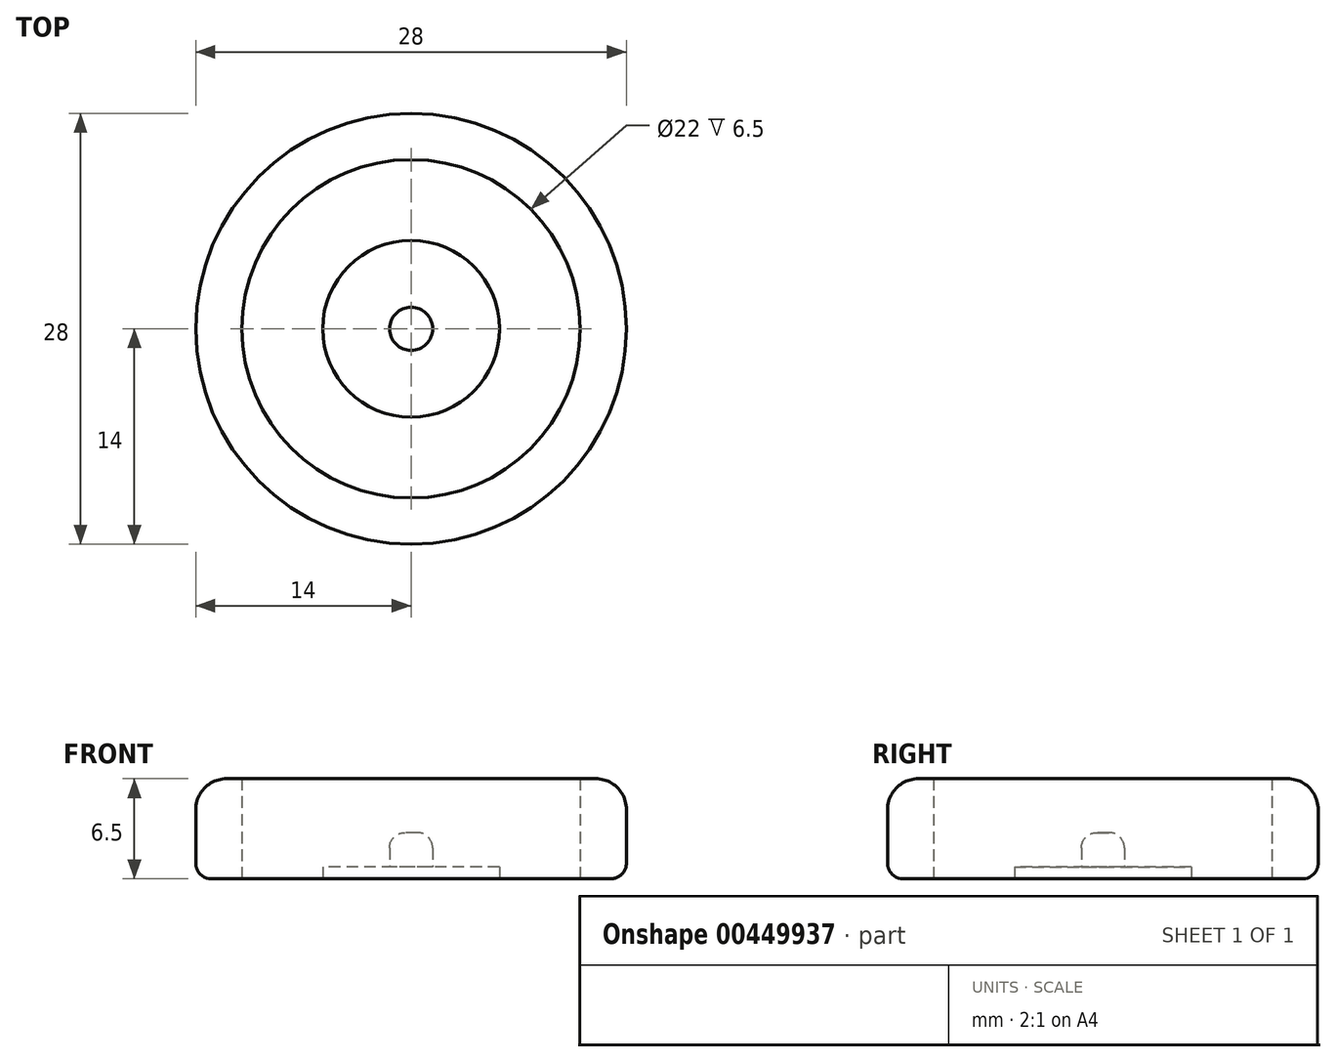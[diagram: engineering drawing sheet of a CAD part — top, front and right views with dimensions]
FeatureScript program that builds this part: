
annotation { "Feature Type Name" : "Feature", "Feature Type Description" : "" }
export const myFeature = defineFeature(function(context is Context, id is Id, definition is map)
    precondition{}
    {
        {
            var Q0;
            Q0=qCreatedBy(makeId("Top.planeOp"),FACE);
            var sketch = newSketch(context, id + "F0", { "sketchPlane" : qUnion([Q0])});
            skCircle(sketch, "E0", {"center": v(0, 0) * mm, "radius": 11 * mm});
            skCircle(sketch, "E1", {"center": v(0, 0) * mm, "radius": 14 * mm});
            skSolve(sketch);
        }
        {
            var Q0;
            Q0=makeQuery(id+"F0.imprint","IMPRINT",FACE,{"disambiguationData":[TD([[makeQuery(id+"F0.imprint","IMPRINT",EDGE,{"derivedFrom":sQuery(id+"F0.wireOp",EDGE,"E0")}),-1.0]])]});
            extrude(context, id + "F1", {"entities" : qUnion([Q0]), "depth" : 6.5 * mm});
        }
        {
            var Q0;
            Q0=makeQuery(id+"F1.opExtrude","CAP_EDGE",EDGE,{"disambiguationData":[OSD([sQuery(id+"F0.wireOp",EDGE,"E1")])],"isStart":false});
            fillet(context, id + "F2", {"entities" : qUnion([Q0]), "radius" : 2 * mm, "tangentPropagation" : true, "allowEdgeOverflow" : false});
        }
        {
            var Q0;
            Q0=makeQuery(id+"F1.opExtrude","CAP_EDGE",EDGE,{"disambiguationData":[OSD([sQuery(id+"F0.wireOp",EDGE,"E1")])],"isStart":true});
            fillet(context, id + "F3", {"entities" : qUnion([Q0]), "radius" : 1 * mm, "tangentPropagation" : true, "allowEdgeOverflow" : false});
        }
        {
            var Q0;
            Q0=qCreatedBy(makeId("Top.planeOp"),FACE);
            var sketch = newSketch(context, id + "F4", { "sketchPlane" : qUnion([Q0])});
            skCircle(sketch, "E2", {"center": v(0, 0) * mm, "radius": 5.75 * mm});
            skCircle(sketch, "E3", {"center": v(0, 0) * mm, "radius": 1.4 * mm});
            skSolve(sketch);
        }
        {
            var Q0;
            Q0=makeQuery(id+"F4.imprint","IMPRINT",FACE,{"disambiguationData":[TD([[makeQuery(id+"F4.imprint","IMPRINT",EDGE,{"derivedFrom":sQuery(id+"F4.wireOp",EDGE,"E2")}),1.0]])]});
            extrude(context, id + "F5", {"entities" : qUnion([Q0]), "depth" : .75 * mm});
        }
        {
            var Q0;
            Q0=makeQuery(id+"F4.imprint","IMPRINT",FACE,{"disambiguationData":[TD([[makeQuery(id+"F4.imprint","IMPRINT",EDGE,{"derivedFrom":sQuery(id+"F4.wireOp",EDGE,"E3")}),1.0]])]});
            extrude(context, id + "F6", {"entities" : qUnion([Q0]), "operationType" : NewBodyOperationType.ADD, "depth" : 3 * mm});
        }
        {
            var Q0;
            Q0=makeQuery(id+"F6.opExtrude","CAP_EDGE",EDGE,{"disambiguationData":[OSD([sQuery(id+"F4.wireOp",EDGE,"E3")])],"isStart":false});
            fillet(context, id + "F7", {"entities" : qUnion([Q0]), "radius" : 1 * mm, "tangentPropagation" : true, "allowEdgeOverflow" : false});
        }
    });
